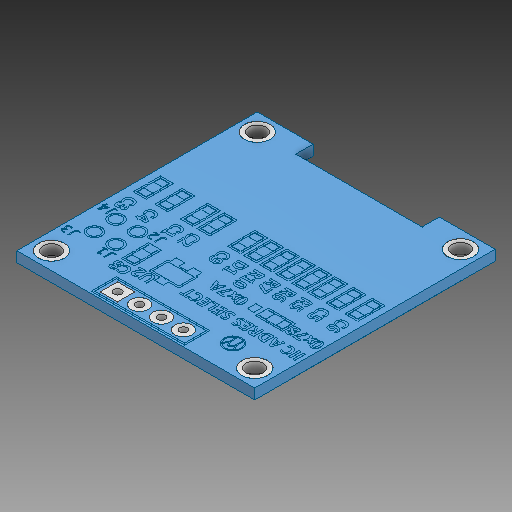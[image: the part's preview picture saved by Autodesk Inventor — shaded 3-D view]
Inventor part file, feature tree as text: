
AUTODESK INVENTOR PART (.ipt)
format: ipt  version: 2020 (Build 240168000, 168)  size: 2,579,456 bytes
history: native  units: mm
features: other x11, hole x7
ambient origin geometry x8: Origin, YZ Plane, XZ Plane, XY Plane, X Axis, Y Axis, Z Axis, Center Point
bodies: Body1 (feature_tree), Body2 (feature_tree), Body3 (feature_tree), Body4 (feature_tree), Body5 (feature_tree), Body6 (feature_tree), Body7 (feature_tree), Body8 (feature_tree), Body9 (feature_tree)
feature tree (18):
  other  "Твердое тело1"
  other  "Твердое тело2"
  other  "Твердое тело3"
  other  "Твердое тело4"
  other  "Твердое тело5"
  other  "Твердое тело6"
  other  "Твердое тело7"
  other  "Твердое тело8"
  other  "Твердое тело9"
  other  "board_body"
  other  "Body 97"
  hole  "hole"  [1 undecoded]
  hole  "hole1"  [1 undecoded]
  hole  "hole3"  [1 undecoded]
  hole  "hole4"  [1 undecoded]
  hole  "hole5"  [1 undecoded]
  hole  "hole6"  [1 undecoded]
  hole  "hole7"  [1 undecoded]
note: 7 required parameter values undecoded (feature->parameter linkage not recoverable at this tier; creation-order binding heuristic only, values carry confidence <= 0.55)
